# Revit family: 111210017132734
name_source: partatom
category: Modelos genéricos
revit_build: Autodesk Revit 2018 (Build: 20190510_1515(x64)
units: mm (PartAtom-declared; Revit-internal decimal feet)

## family parameters
Compartido = No
Corte con vacíos al cargar = No
Cota de conector redondo = Diámetro de uso
Puede alojar armadura = No
Punto de cálculo de habitación = No
Se basa en plano de trabajo = No
Siempre vertical = No
Tipo de pieza = Normal

## types (1)
- CUBREJUNTA TERMINAL PVC 40MM GRIS ROLLO 50MT
    Alto = 5 mm  [stored 0.0164042 ft]
    Aplicacion = ENTRE JUNTAS
    Color = GRIS
    Descripción = Cubrejunta Terminal  40 MM.
    Dimension = 40 mm  [stored 0.131234 ft]
    Dureza = Shore A 80
    Empresa = CNP SPA.
    Espesor = 3 mm  [stored 0.00984252 ft]
    Largo = 1200 mm
    Material = PVC flexible gris
    Modelo = CUBREJUNTA TERMINAL PVC 40MM
    Nombre SKU = CUBREJUNTA TERMINAL PVC 40MM GRIS ROLLO 50MT
    Num SKUs = 111210017132734
    URL = https://www.empresascnp.cl
    Unidad = Perfil Superior (Rollos de 50 Mts)
    Url Ficha tecnica = https://empresascnp.cl
    Uso = Se utiliza para unir distintas superficies con diferencias de niveles, siendo un
producto que permite compensar estas diferencias al unir alfombras, piso laminado,
Cerámica, entre otros.
    Ventajas = Autoextinguible

note: [stored X ft] marks values corroborated as IEEE doubles in the binary element streams (Revit-internal decimal feet)

## geometry (parser evidence)
native form markers: Sweep x2
no freeform markers — native parametric forms only
